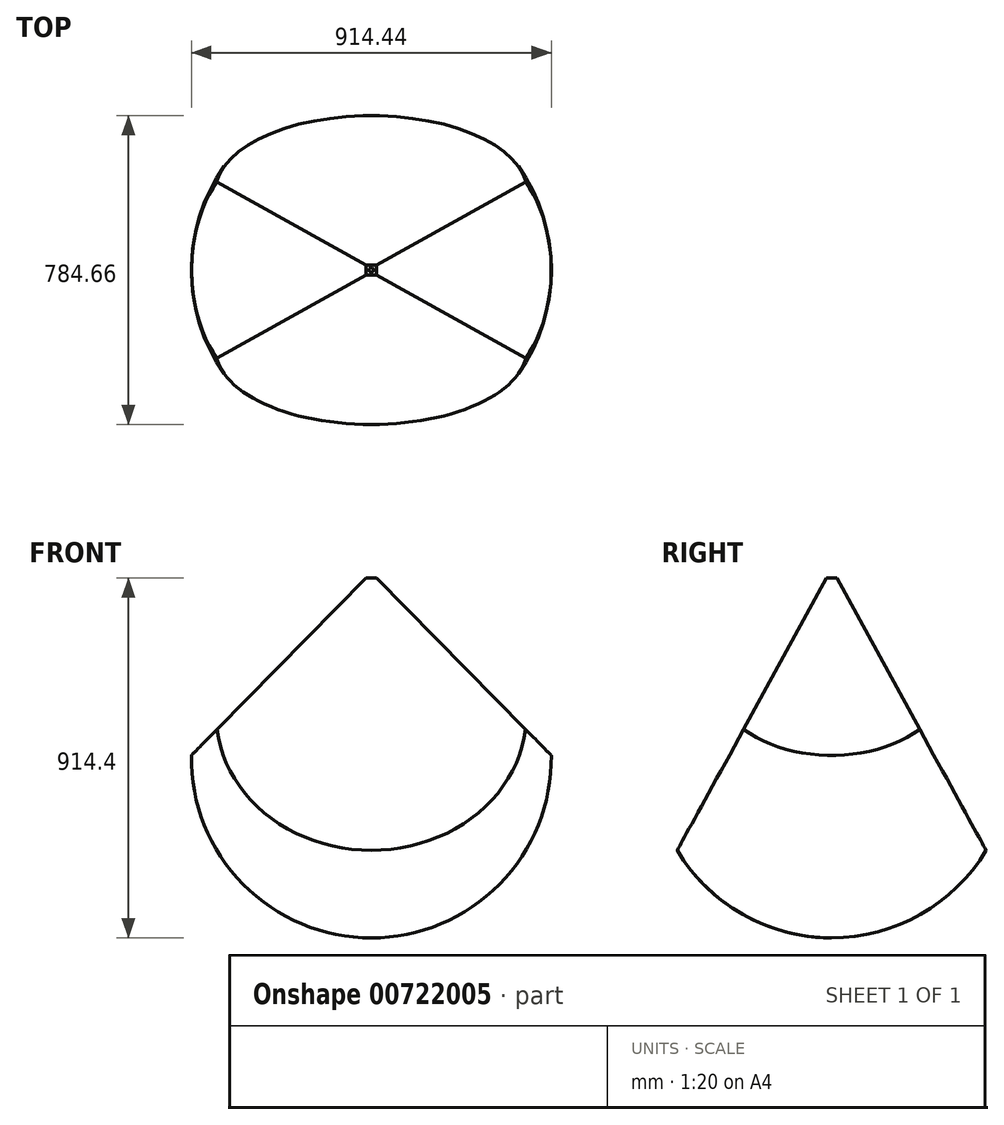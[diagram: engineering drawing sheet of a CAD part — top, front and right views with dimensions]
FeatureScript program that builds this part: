
annotation { "Feature Type Name" : "Feature", "Feature Type Description" : "" }
export const myFeature = defineFeature(function(context is Context, id is Id, definition is map)
    precondition{}
    {
        {
            var Q0;
            Q0=qCreatedBy(makeId("Top.planeOp"),FACE);
            var sketch = newSketch(context, id + "F0", { "sketchPlane" : qUnion([Q0])});
            skLineSegment(sketch, "E0.bottom", {"start": v(-914.4, 514.35) * mm, "end": v(914.4, 514.35) * mm});
            skLineSegment(sketch, "E0.top", {"start": v(-914.4, -514.35) * mm, "end": v(914.4, -514.35) * mm});
            skLineSegment(sketch, "E0.left", {"start": v(-914.4, 514.35) * mm, "end": v(-914.4, -514.35) * mm});
            skLineSegment(sketch, "E0.right", {"start": v(914.4, 514.35) * mm, "end": v(914.4, -514.35) * mm});
            skPoint(sketch, "E1", {"position": v(0, 514.35) * mm});
            skPoint(sketch, "E2", {"position": v(-914.4, 0) * mm});
            skSolve(sketch);
        }
        {
            var Q0;
            Q0=qCreatedBy(makeId("Top.planeOp"),FACE);
            cPlane(context, id + "F1", {"entities" : qUnion([Q0]), "cplaneType" : CPlaneType.OFFSET, "offset" : 914.4 * mm, "width" : 152.4 * mm, "height" : 152.4 * mm});
        }
        {
            var Q0;
            Q0=qCreatedBy(id+"F1.planeOp",FACE);
            var sketch = newSketch(context, id + "F2", { "sketchPlane" : qUnion([Q0])});
            skLineSegment(sketch, "E3.bottom", {"start": v(-12.7, 12.7) * mm, "end": v(12.7, 12.7) * mm});
            skLineSegment(sketch, "E3.top", {"start": v(-12.7, -12.7) * mm, "end": v(12.7, -12.7) * mm});
            skLineSegment(sketch, "E3.left", {"start": v(-12.7, 12.7) * mm, "end": v(-12.7, -12.7) * mm});
            skLineSegment(sketch, "E3.right", {"start": v(12.7, 12.7) * mm, "end": v(12.7, -12.7) * mm});
            skPoint(sketch, "E4", {"position": v(0, 12.7) * mm});
            skPoint(sketch, "E5", {"position": v(12.7, 0) * mm});
            skSolve(sketch);
        }
        {
            var Q0;
            Q0=makeQuery(id+"F2.imprint","IMPRINT",FACE,{"disambiguationData":[TD([[makeQuery(id+"F2.imprint","IMPRINT",EDGE,{"derivedFrom":sQuery(id+"F2.wireOp",EDGE,"E3.bottom")}),-1.0]])]});
            var Q1;
            Q1=makeQuery(id+"F0.imprint","IMPRINT",FACE,{"disambiguationData":[TD([[makeQuery(id+"F0.imprint","IMPRINT",EDGE,{"derivedFrom":sQuery(id+"F0.wireOp",EDGE,"E0.bottom")}),-1.0]])]});
            loft(context, id + "F3", {"sheetProfilesArray" : [{ "sheetProfileEntities" : qUnion([Q0]) }, { "sheetProfileEntities" : qUnion([Q1]) }]});
        }
        {
            var Q0;
            Q0=qCreatedBy(makeId("Right.planeOp"),FACE);
            var sketch = newSketch(context, id + "F4", { "sketchPlane" : qUnion([Q0])});
            skLineSegment(sketch, "E6", {"start": v(0, 914.44) * mm, "end": v(0, 0) * mm});
            skPoint(sketch, "E7", {"position": v(0, 457.22) * mm});
            skArc(sketch, "E8", {"start": v(0, 0) * mm, "mid": v(457.22, 457.22) * mm, "end": v(0, 914.44) * mm});
            skSolve(sketch);
        }
        {
            var Q0;
            Q0=makeQuery(id+"F4.imprint","IMPRINT",FACE,{"disambiguationData":[TD([[makeQuery(id+"F4.imprint","IMPRINT",EDGE,{"derivedFrom":sQuery(id+"F4.wireOp",EDGE,"E6")}),1.0]])]});
            var Q1;
            Q1=sQuery(id+"F4.wireOp",EDGE,"E6");
            revolve(context, id + "F5", {"operationType" : NewBodyOperationType.INTERSECT, "surfaceOperationType" : NewSurfaceOperationType.NEW, "entities" : qUnion([Q0]), "axis" : qUnion([Q1]), "revolveType" : RevolveType.FULL});
        }
    });
